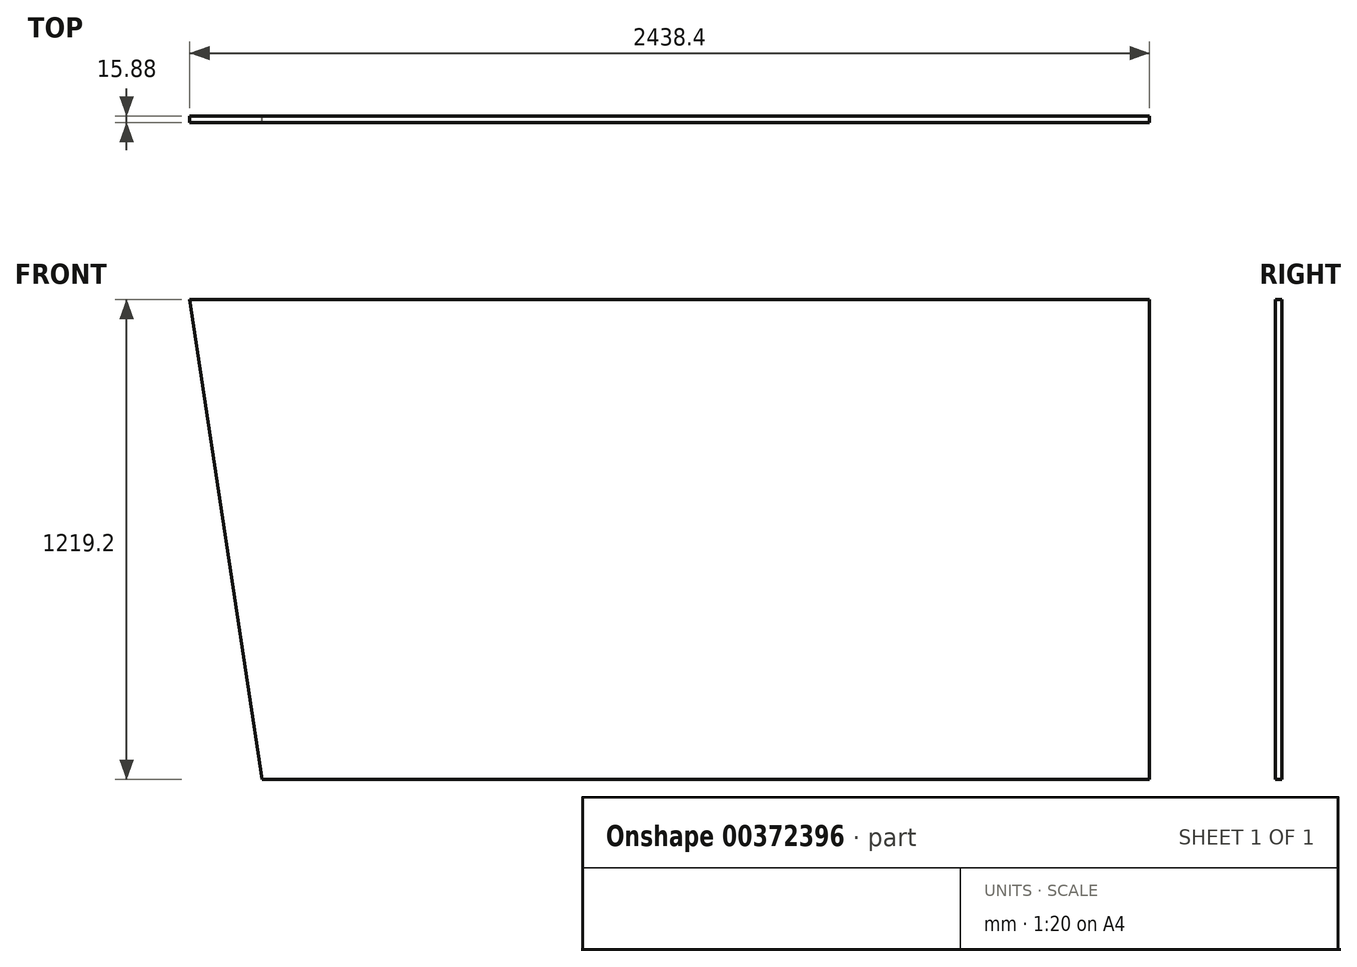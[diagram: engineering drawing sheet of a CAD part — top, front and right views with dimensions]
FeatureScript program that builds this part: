
annotation { "Feature Type Name" : "Feature", "Feature Type Description" : "" }
export const myFeature = defineFeature(function(context is Context, id is Id, definition is map)
    precondition{}
    {
        {
            var Q0;
            Q0=qCreatedBy(makeId("Front.planeOp"),FACE);
            var sketch = newSketch(context, id + "F0", { "sketchPlane" : qUnion([Q0])});
            skLineSegment(sketch, "E0.bottom", {"start": v(1219.2, -609.6) * mm, "end": v(-1035.05, -609.6) * mm});
            skLineSegment(sketch, "E0.top", {"start": v(1219.2, 609.6) * mm, "end": v(-1219.2, 609.6) * mm});
            skLineSegment(sketch, "E0.left", {"start": v(1219.2, -609.6) * mm, "end": v(1219.2, 609.6) * mm});
            skPoint(sketch, "E0.middle", {"position": v(0, 0) * mm});
            skLineSegment(sketch, "E1", {"start": v(-1219.2, 609.6) * mm, "end": v(-1035.05, -609.6) * mm});
            skPoint(sketch, "E2.orphan", {"position": v(-1219.2, -609.6) * mm});
            skSolve(sketch);
        }
        {
            var Q0;
            Q0=qSketchRegion(id+"F0",true);
            extrude(context, id + "F1", {"entities" : qUnion([Q0]), "depth" : 15.88 * mm});
        }
    });
